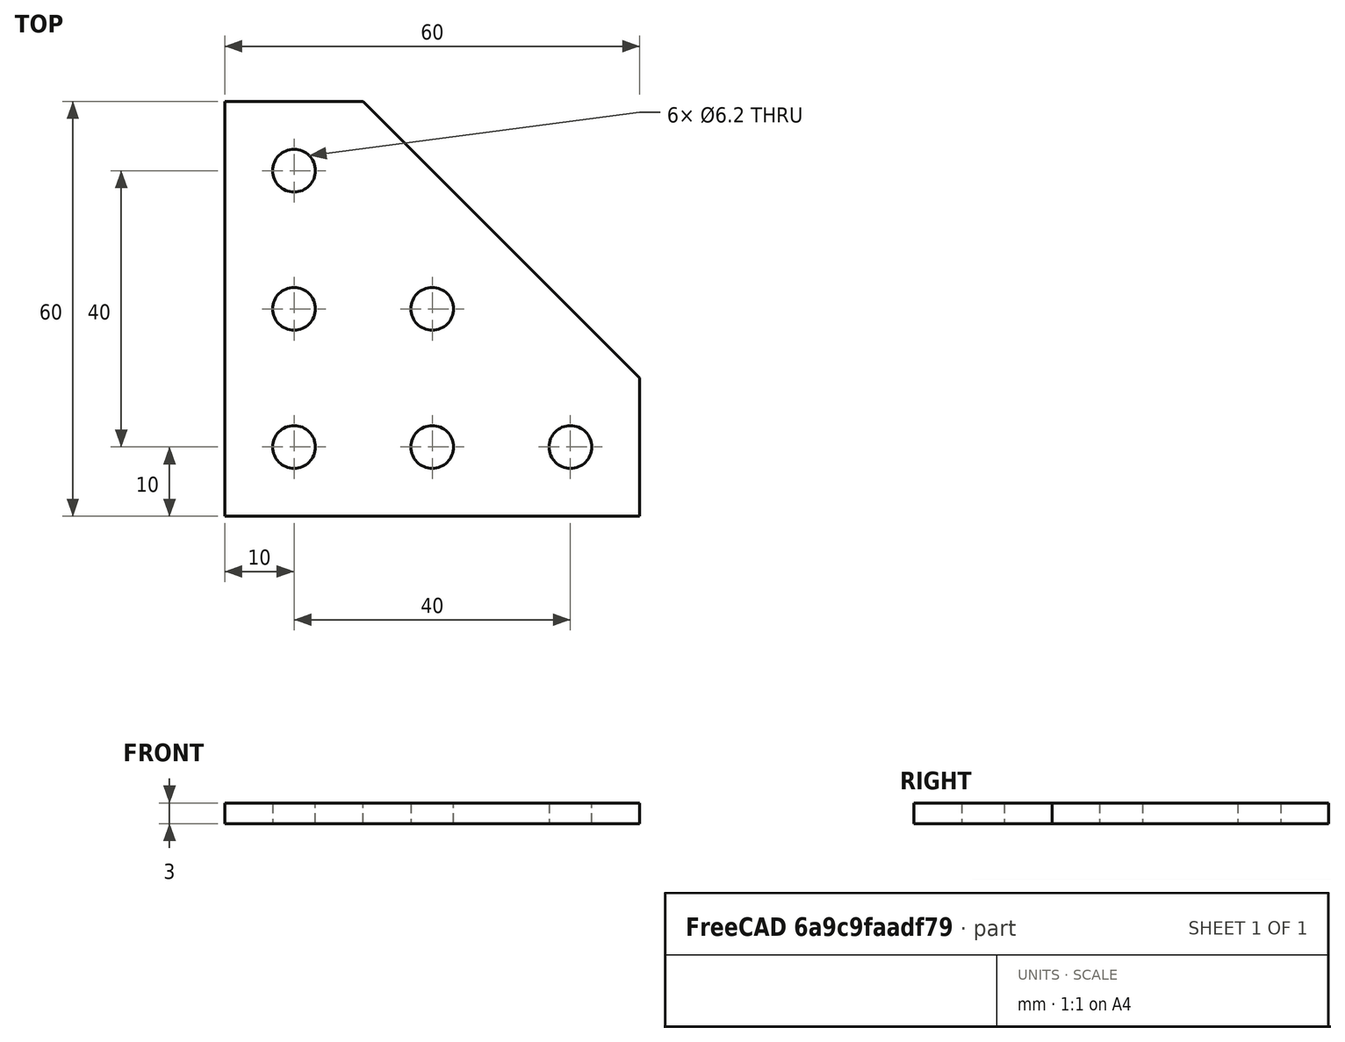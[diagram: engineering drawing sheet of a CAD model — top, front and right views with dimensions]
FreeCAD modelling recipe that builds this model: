
FCSTD DOCUMENT  (FreeCAD 0.19R23964 (Git))
Label: lcon
License: All rights reserved
LicenseURL: http://en.wikipedia.org/wiki/All_rights_reserved
objects: TechDraw::DrawViewDimension×12, TechDraw::DrawViewPart×2, Sketcher::SketchObject×1, PartDesign::Pad×1, PartDesign::Body×1, TechDraw::DrawSVGTemplate×1, TechDraw::DrawViewAnnotation×1, TechDraw::DrawPage×1
note: 4 computed .brp shape members not serialized (recipe doc carries the construction recipe); baked Part::Feature solids carry a one-line shape summary decoded from their .brp

FEATURE [Sketcher::SketchObject] Sketch
  FullyConstrained = true
  MapMode = 5
  Support = -> [XY_Plane]
  sketch-geometry (11):
    g0: LineSegment StartX=0 StartY=60 StartZ=0 EndX=20 EndY=60 EndZ=0
    g1: LineSegment StartX=20 StartY=60 StartZ=0 EndX=60 EndY=20 EndZ=0
    g2: LineSegment StartX=60 StartY=20 StartZ=0 EndX=60 EndY=0 EndZ=0
    g3: LineSegment StartX=60 StartY=0 StartZ=0 EndX=0 EndY=0 EndZ=0
    g4: LineSegment StartX=0 StartY=0 StartZ=0 EndX=0 EndY=60 EndZ=0
    g5: Circle CenterX=10 CenterY=10 CenterZ=0 NormalX=0 NormalY=0 NormalZ=1 AngleXU=0 Radius=3.1
    g6: Circle CenterX=10 CenterY=30 CenterZ=0 NormalX=0 NormalY=0 NormalZ=1 AngleXU=0 Radius=3.1
    g7: Circle CenterX=10 CenterY=50 CenterZ=0 NormalX=0 NormalY=0 NormalZ=1 AngleXU=0 Radius=3.1
    g8: Circle CenterX=30 CenterY=10 CenterZ=0 NormalX=0 NormalY=0 NormalZ=1 AngleXU=0 Radius=3.1
    g9: Circle CenterX=50 CenterY=10 CenterZ=0 NormalX=0 NormalY=0 NormalZ=1 AngleXU=0 Radius=3.1
    g10: Circle CenterX=30 CenterY=30 CenterZ=0 NormalX=0 NormalY=0 NormalZ=1 AngleXU=0 Radius=3.1
  constraints (32):
    c: Coincident(g0,g1)
    c: Coincident(g1,g2)
    c: Coincident(g2,g3)
    c: Coincident(g3,g4)
    c: Coincident(g4,g0)
    c: Coincident(g3,g-1)
    c: DistanceX(g-1,g2) = 60
    c: DistanceY(g-1,g0) = 60
    c: DistanceX(g-1,g1) = 60
    c: DistanceX(g-1,g0) = 20
    c: DistanceY(g-1,g0) = 60
    c: DistanceY(g-1,g1) = 20
    c: DistanceX(g0,g-1) = 0
    c: DistanceY(g2,g-1) = 0
    c: DistanceX(g-1,g5) = 10
    c: DistanceX(g-1,g6) = 10
    c: DistanceX(g-1,g7) = 10
    c: DistanceY(g-1,g5) = 10
    c: DistanceY(g-1,g6) = 30
    c: DistanceY(g-1,g7) = 50
    c: DistanceY(g-1,g8) = 10
    c: DistanceY(g-1,g10) = 30
    c: DistanceY(g-1,g9) = 10
    c: DistanceX(g-1,g9) = 50
    c: DistanceX(g-1,g8) = 30
    c: Radius(g7) = 3.1
    c: Radius(g6) = 3.1
    c: Radius(g10) = 3.1
    c: Radius(g5) = 3.1
    c: Radius(g8) = 3.1
    c: Radius(g9) = 3.1
    c: DistanceX(g-1,g10) = 30
FEATURE [PartDesign::Pad] Pad
  AllowMultiFace = false
  Direction = (1,1,1)
  Length = 3
  Length2 = 100
  Profile = -> Sketch
  Refine = true
  Type = 0
FEATURE [PartDesign::Body] Body
  Group = -> [Sketch,Pad]
  Origin = -> BodyOrigin
  Tip = -> Pad
FEATURE [TechDraw::DrawSVGTemplate] Template
  EditableTexts =  =Links two Profiles;   =at the ends; Approved By=Oliver Schlüter; Classification=CLASSIFICATION; Created By=Lukas Schattenhofer; Date Of Issue=07.07.2021; Document Status=Checked; Document Type=Technical drawing; Identification Number=IDENTIFICATION NUMBER; Legal Owner=OSE Germany; Project name=UniProKit-Lib; Rev=REV; Scale=1:1; Seg=0/0; Technical Reference=TECHNICAL REFERENCE; Title/Supplementary Title=lcon - Verbinder
  Height = 210
  Orientation = 1
  Width = 297
FEATURE [TechDraw::DrawViewPart] View001
  CoarseView = false
  Direction = (-1,0,0)
  Focus = 100
  HardHidden = false
  IsoCount = 0
  IsoHidden = false
  IsoVisible = false
  LockPosition = false
  Perspective = false
  Rotation = 0
  ScaleType = 0
  SeamHidden = false
  SeamVisible = true
  SmoothHidden = false
  SmoothVisible = true
  Source = -> [Pad]
  X = 204.113
  XDirection = (0,0,-1)
  Y = 137.877
FEATURE [TechDraw::DrawViewDimension] Dimension015
  Arbitrary = false
  ArbitraryTolerances = false
  EqualTolerance = true
  FormatSpec = %.2f
  FormatSpecOverTolerance = %+.2f
  FormatSpecUnderTolerance = %+.2f
  Inverted = false
  LockPosition = false
  MeasureType = 1
  OverTolerance = 0
  References2D = -> [View001]
  Rotation = 0
  ScaleType = 0
  TheoreticalExact = false
  Type = 0
  UnderTolerance = 0
  X = 10.5298
  Y = 45.4187
FEATURE [TechDraw::DrawViewAnnotation] Annotation
  Font = osifont
  LineSpace = 80
  LockPosition = false
  MaxWidth = -1
  Rotation = 0
  ScaleType = 0
  Text = All wholes have a radius of 3,10mm | Material: Aluminium, ABS, PLA (depending on desired strenght
  TextSize = 5
  TextStyle = 0
  X = 206.66
  Y = 62.4282
FEATURE [TechDraw::DrawViewPart] View002
  CoarseView = false
  Direction = (0,0,1)
  Focus = 100
  HardHidden = false
  IsoCount = 0
  IsoHidden = false
  IsoVisible = false
  LockPosition = false
  Perspective = false
  Rotation = 0
  ScaleType = 0
  SeamHidden = false
  SeamVisible = true
  SmoothHidden = false
  SmoothVisible = true
  Source = -> [Pad]
  X = 108.741
  XDirection = (1,0,0)
  Y = 139.838
FEATURE [TechDraw::DrawViewDimension] Dimension016
  Arbitrary = false
  ArbitraryTolerances = false
  EqualTolerance = true
  FormatSpec = %.2f
  FormatSpecOverTolerance = %+.2f
  FormatSpecUnderTolerance = %+.2f
  Inverted = false
  LockPosition = false
  MeasureType = 1
  OverTolerance = 0
  References2D = -> [View002]
  Rotation = 0
  ScaleType = 0
  TheoreticalExact = false
  Type = 0
  UnderTolerance = 0
  X = -13.5838
  Y = -34.9793
FEATURE [TechDraw::DrawViewDimension] Dimension017
  Arbitrary = false
  ArbitraryTolerances = false
  EqualTolerance = true
  FormatSpec = %.2f
  FormatSpecOverTolerance = %+.2f
  FormatSpecUnderTolerance = %+.2f
  Inverted = false
  LockPosition = false
  MeasureType = 1
  OverTolerance = 0
  References2D = -> [View002]
  Rotation = 0
  ScaleType = 0
  TheoreticalExact = false
  Type = 0
  UnderTolerance = 0
  X = -13.7315
  Y = -44.4928
FEATURE [TechDraw::DrawViewDimension] Dimension018
  Arbitrary = false
  ArbitraryTolerances = false
  EqualTolerance = true
  FormatSpec = %.2f
  FormatSpecOverTolerance = %+.2f
  FormatSpecUnderTolerance = %+.2f
  Inverted = false
  LockPosition = false
  MeasureType = 1
  OverTolerance = 0
  References2D = -> [View002]
  Rotation = 0
  ScaleType = 0
  TheoreticalExact = false
  Type = 0
  UnderTolerance = 0
  X = -4.04865
  Y = -54.0063
FEATURE [TechDraw::DrawViewDimension] Dimension019
  Arbitrary = false
  ArbitraryTolerances = false
  EqualTolerance = true
  FormatSpec = %.2f
  FormatSpecOverTolerance = %+.2f
  FormatSpecUnderTolerance = %+.2f
  Inverted = false
  LockPosition = false
  MeasureType = 1
  OverTolerance = 0
  References2D = -> [View002]
  Rotation = 0
  ScaleType = 0
  TheoreticalExact = false
  Type = 0
  UnderTolerance = 0
  X = 1.9027
  Y = -62.663
FEATURE [TechDraw::DrawViewDimension] Dimension021
  Arbitrary = false
  ArbitraryTolerances = false
  EqualTolerance = true
  FormatSpec = %.2f
  FormatSpecOverTolerance = %+.2f
  FormatSpecUnderTolerance = %+.2f
  Inverted = false
  LockPosition = false
  MeasureType = 1
  OverTolerance = 0
  References2D = -> [View002]
  Rotation = 0
  ScaleType = 0
  TheoreticalExact = false
  Type = 0
  UnderTolerance = 0
  X = -53.8567
  Y = -12.1459
FEATURE [TechDraw::DrawViewDimension] Dimension022
  Arbitrary = false
  ArbitraryTolerances = false
  EqualTolerance = true
  FormatSpec = %.2f
  FormatSpecOverTolerance = %+.2f
  FormatSpecUnderTolerance = %+.2f
  Inverted = false
  LockPosition = false
  MeasureType = 1
  OverTolerance = 0
  References2D = -> [View002]
  Rotation = 0
  ScaleType = 0
  TheoreticalExact = false
  Type = 0
  UnderTolerance = 0
  X = -66.0567
  Y = -4.04865
FEATURE [TechDraw::DrawViewDimension] Dimension023
  Arbitrary = false
  ArbitraryTolerances = false
  EqualTolerance = true
  FormatSpec = %.2f
  FormatSpecOverTolerance = %+.2f
  FormatSpecUnderTolerance = %+.2f
  Inverted = false
  LockPosition = false
  MeasureType = 1
  OverTolerance = 0
  References2D = -> [View002]
  Rotation = 0
  ScaleType = 0
  TheoreticalExact = false
  Type = 0
  UnderTolerance = 0
  X = -78.5189
  Y = -1.9027
FEATURE [TechDraw::DrawViewDimension] Dimension024
  Arbitrary = false
  ArbitraryTolerances = false
  EqualTolerance = true
  FormatSpec = %.2f
  FormatSpecOverTolerance = %+.2f
  FormatSpecUnderTolerance = %+.2f
  Inverted = false
  LockPosition = false
  MeasureType = 1
  OverTolerance = 0
  References2D = -> [View002]
  Rotation = 0
  ScaleType = 0
  TheoreticalExact = false
  Type = 0
  UnderTolerance = 0
  X = -36.2477
  Y = -6.60723
FEATURE [TechDraw::DrawViewDimension] Dimension026
  Arbitrary = false
  ArbitraryTolerances = false
  EqualTolerance = true
  FormatSpec = R%.2f
  FormatSpecOverTolerance = %+.2f
  FormatSpecUnderTolerance = %+.2f
  Inverted = false
  LockPosition = false
  MeasureType = 1
  OverTolerance = 0
  References2D = -> [View002]
  Rotation = 0
  ScaleType = 0
  TheoreticalExact = false
  Type = 4
  UnderTolerance = 0
  X = 40.6439
  Y = 3.47384
FEATURE [TechDraw::DrawViewDimension] Dimension027
  Arbitrary = false
  ArbitraryTolerances = false
  EqualTolerance = true
  FormatSpec = %.2f
  FormatSpecOverTolerance = %+.2f
  FormatSpecUnderTolerance = %+.2f
  Inverted = false
  LockPosition = false
  MeasureType = 1
  OverTolerance = 0
  References2D = -> [View002]
  Rotation = 0
  ScaleType = 0
  TheoreticalExact = false
  Type = 0
  UnderTolerance = 0
  X = 58.8329
  Y = -16.8735
FEATURE [TechDraw::DrawViewDimension] Dimension028
  Arbitrary = false
  ArbitraryTolerances = false
  EqualTolerance = true
  FormatSpec = %.2f
  FormatSpecOverTolerance = %+.2f
  FormatSpecUnderTolerance = %+.2f
  Inverted = false
  LockPosition = false
  MeasureType = 1
  OverTolerance = 0
  References2D = -> [View002]
  Rotation = 0
  ScaleType = 0
  TheoreticalExact = false
  Type = 0
  UnderTolerance = 0
  X = -20.3474
  Y = 46.6744
FEATURE [TechDraw::DrawPage] Page  label="Technical Drawing"
  KeepUpdated = true
  NextBalloonIndex = 2
  ProjectionType = 0
  Template = -> Template
  Views = -> [View001,Dimension015,Annotation,View002,Dimension016,Dimension017,Dimension018,Dimension019,Dimension021,Dimension022,Dimension023,Dimension024,Dimension026,Dimension027,Dimension028]
